# Revit family: Tripod_table_lamp_HM9 New
name_source: partatom
category: Furniture
units: mm (PartAtom-declared; Revit-internal decimal feet)

## family parameters
Always vertical = Yes
Cut with Voids When Loaded = No
Enable Cutting in Views = No
OmniClass Number = 23.40.20.00
OmniClass Title = General Furniture and Specialties
Render Appearance Source = Family Geometry
Room Calculation Point = No
Shared = No
Work Plane-Based = No

## types (1)
- Tripod_table_lamp_HM9 New
    Cord = &tradition Textile Black
    Default Elevation = 0 mm  [stored 0 ft]
    Depth = 33cm/12,6in
    Design = Hvidt & Mølgaard
    Design Year = 1953
    Height = 45cm/17,7in
    Inner Shade = &tradition Powder Coated Steel White 9010 Semi Matt Finish
    Manufacturer = &Tradition
    Model = HM9 Tripod
    Packaging dimensions & weight = Please see product fact sheet available from download page on website
    Shade and base = &tradition Powder Coated Metal black matt
    Type Comments = Tripod
    URL = https://www.andtradition.com
    Variation = Please visit our website to see available colours and finishes.
    Width = 26cm/10,2in

note: [stored X ft] marks values corroborated as IEEE doubles in the binary element streams (Revit-internal decimal feet)

## geometry (parser evidence)
native form markers: Sweep x3
no freeform markers — native parametric forms only
